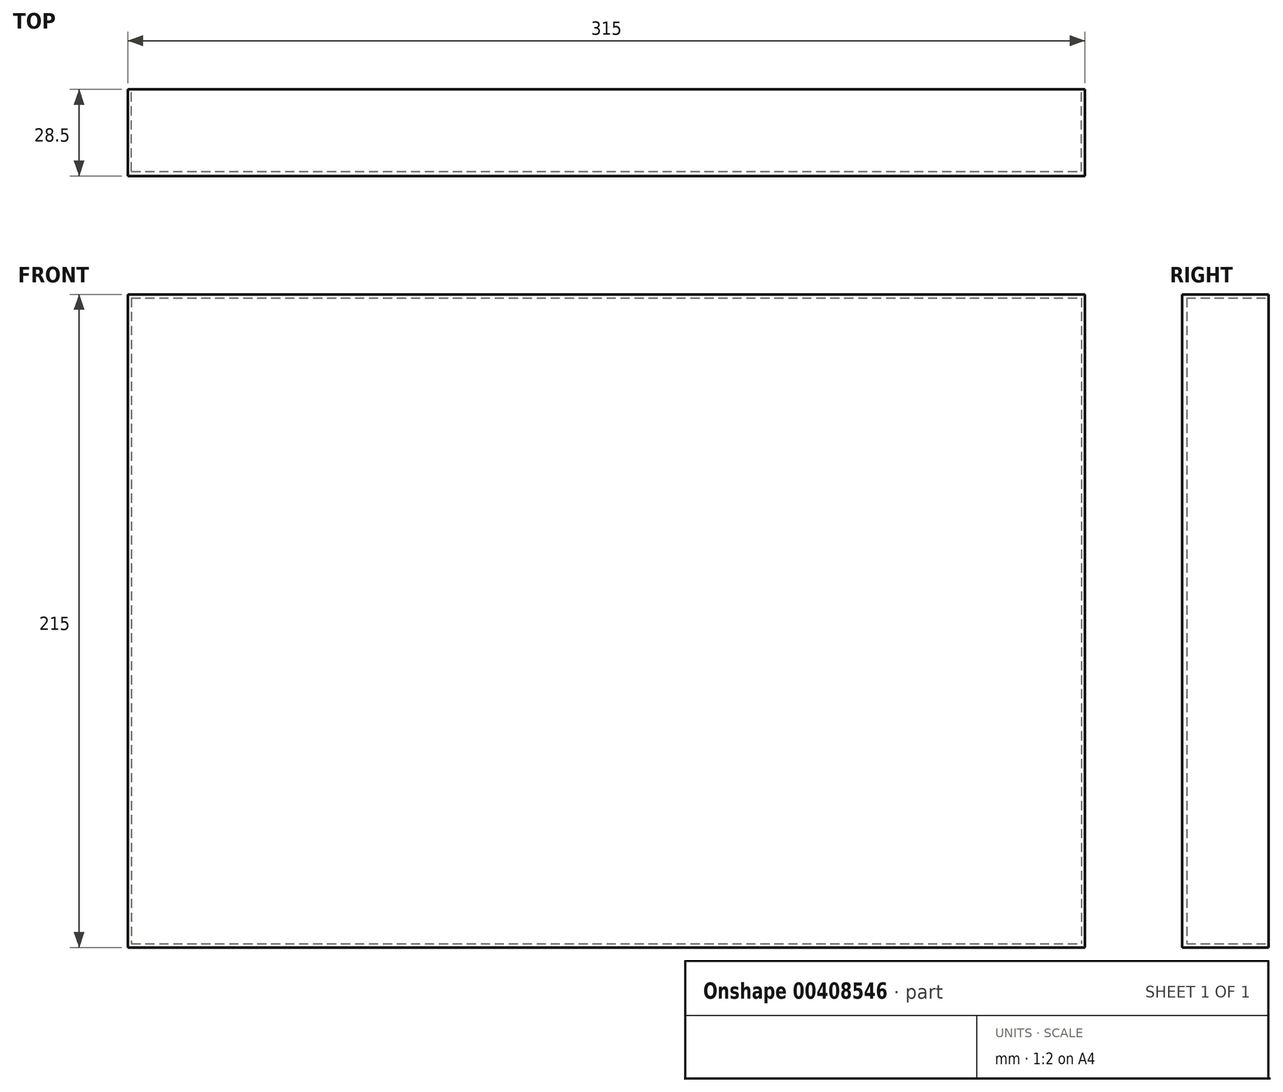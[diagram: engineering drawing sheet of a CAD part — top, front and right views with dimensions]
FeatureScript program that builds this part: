
annotation { "Feature Type Name" : "Feature", "Feature Type Description" : "" }
export const myFeature = defineFeature(function(context is Context, id is Id, definition is map)
    precondition{}
    {
        {
            var Q0;
            Q0=qCreatedBy(makeId("Front.planeOp"),FACE);
            var sketch = newSketch(context, id + "F0", { "sketchPlane" : qUnion([Q0])});
            skLineSegment(sketch, "E0.bottom", {"start": v(-165, 106.2) * mm, "end": v(150, 106.2) * mm});
            skLineSegment(sketch, "E0.top", {"start": v(-165, -108.8) * mm, "end": v(150, -108.8) * mm});
            skLineSegment(sketch, "E0.left", {"start": v(-165, 106.2) * mm, "end": v(-165, -108.8) * mm});
            skLineSegment(sketch, "E0.right", {"start": v(150, 106.2) * mm, "end": v(150, -108.8) * mm});
            skLineSegment(sketch, "E1.0", {"start": v(-163.8, 105) * mm, "end": v(148.8, 105) * mm});
            skLineSegment(sketch, "E2.0", {"start": v(-163.8, 105) * mm, "end": v(-163.8, -107.6) * mm});
            skLineSegment(sketch, "E3.0", {"start": v(-163.8, -107.6) * mm, "end": v(148.8, -107.6) * mm});
            skLineSegment(sketch, "E4.0", {"start": v(148.8, 105) * mm, "end": v(148.8, -107.6) * mm});
            skSolve(sketch);
        }
        {
            var Q0;
            Q0=makeQuery(id+"F0.imprint","IMPRINT",FACE,{"disambiguationData":[TD([[makeQuery(id+"F0.imprint","IMPRINT",EDGE,{"derivedFrom":sQuery(id+"F0.wireOp",EDGE,"E0.bottom")}),-1.0]])]});
            extrude(context, id + "F1", {"entities" : qUnion([Q0]), "depth" : 28.5 * mm});
        }
        {
            var Q0;
            Q0=makeQuery(id+"F1.opExtrude","CAP_FACE",FACE,{"disambiguationData":[OSD([sQuery(id+"F0.wireOp",EDGE,"E0.bottom"),sQuery(id+"F0.wireOp",EDGE,"E0.top"),sQuery(id+"F0.wireOp",EDGE,"E0.left"),sQuery(id+"F0.wireOp",EDGE,"E0.right"),sQuery(id+"F0.wireOp",EDGE,"E1.0"),sQuery(id+"F0.wireOp",EDGE,"E2.0"),sQuery(id+"F0.wireOp",EDGE,"E3.0"),sQuery(id+"F0.wireOp",EDGE,"E4.0")])],"isStart":false});
            var sketch = newSketch(context, id + "F2", { "sketchPlane" : qUnion([Q0])});
            skLineSegment(sketch, "E5.bottom", {"start": v(-163.8, 105) * mm, "end": v(148.8, 105) * mm});
            skLineSegment(sketch, "E5.top", {"start": v(-163.8, -107.6) * mm, "end": v(148.8, -107.6) * mm});
            skLineSegment(sketch, "E5.left", {"start": v(-163.8, 105) * mm, "end": v(-163.8, -107.6) * mm});
            skLineSegment(sketch, "E5.right", {"start": v(148.8, 105) * mm, "end": v(148.8, -107.6) * mm});
            skSolve(sketch);
        }
        {
            var Q0;
            Q0=makeQuery(id+"F2.imprint","IMPRINT",FACE,{"disambiguationData":[TD([[makeQuery(id+"F2.imprint","IMPRINT",EDGE,{"derivedFrom":sQuery(id+"F2.wireOp",EDGE,"E5.bottom")}),-1.0]])]});
            extrude(context, id + "F3", {"entities" : qUnion([Q0]), "operationType" : NewBodyOperationType.ADD, "oppositeDirection" : true, "depth" : 1.5 * mm});
        }
    });
